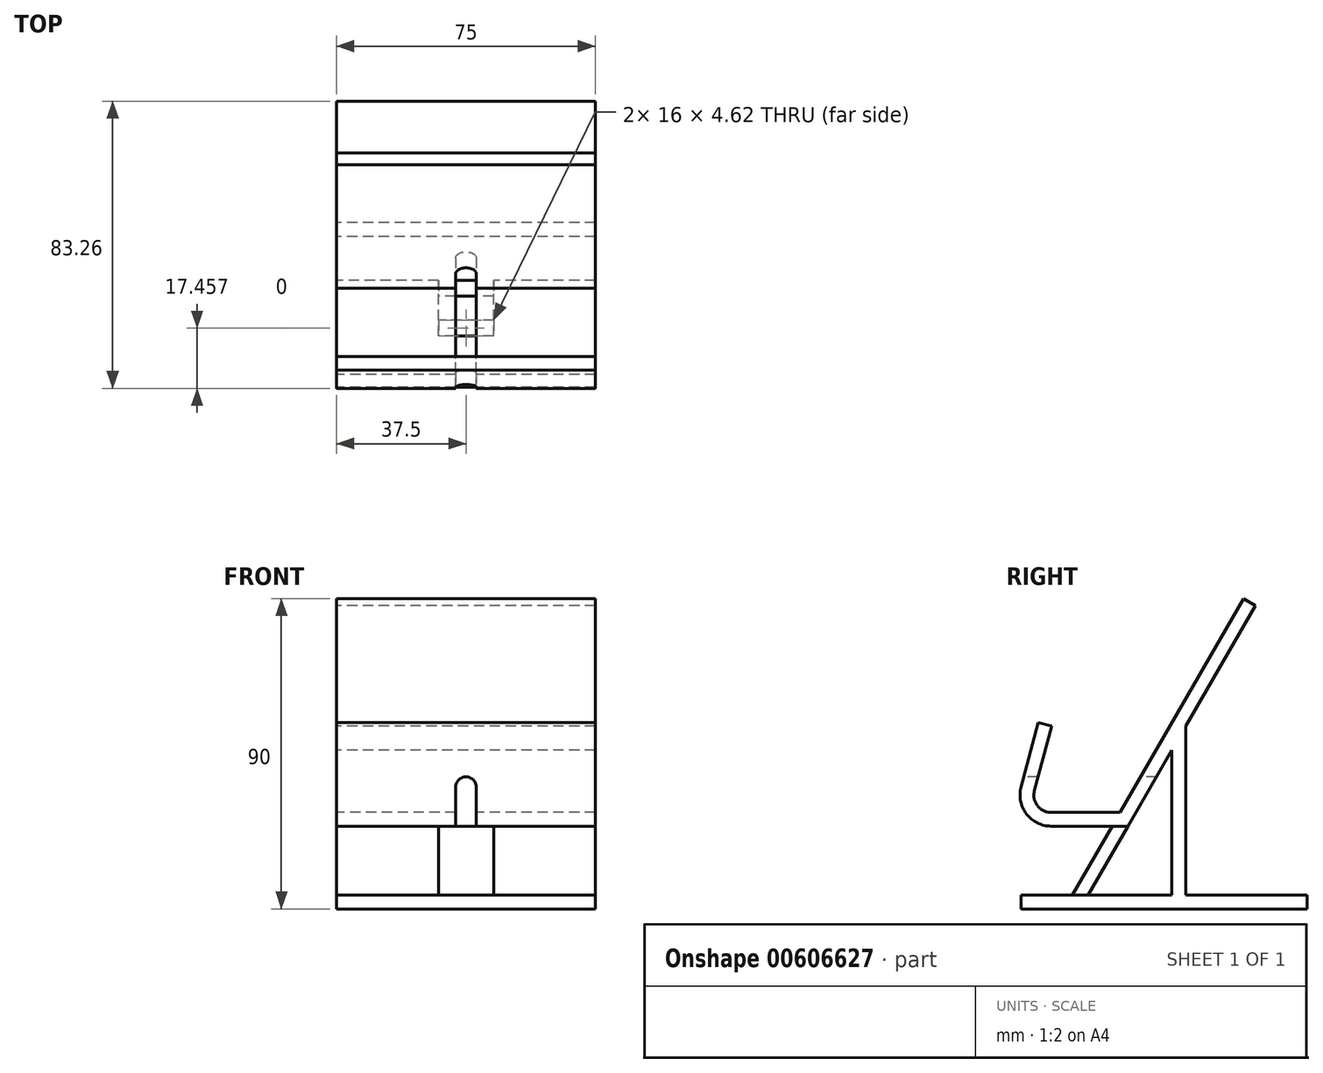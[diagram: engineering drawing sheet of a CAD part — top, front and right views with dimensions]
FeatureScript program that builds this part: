
annotation { "Feature Type Name" : "Feature", "Feature Type Description" : "" }
export const myFeature = defineFeature(function(context is Context, id is Id, definition is map)
    precondition{}
    {
        {
            var Q0;
            Q0=qCreatedBy(makeId("Right.planeOp"),FACE);
            var sketch = newSketch(context, id + "F0", { "sketchPlane" : qUnion([Q0])});
            skLineSegment(sketch, "E0.0", {"start": v(-53.99, -36.2) * mm, "end": v(-48.97, -17.5) * mm});
            skLineSegment(sketch, "E0.1", {"start": v(-29.16, -42.5) * mm, "end": v(-49.16, -42.5) * mm});
            skLineSegment(sketch, "E0.5", {"start": v(-29.16, -42.5) * mm, "end": v(6.64, 19.5) * mm});
            skLineSegment(sketch, "E1.0", {"start": v(-57.85, -35.17) * mm, "end": v(-52.84, -16.47) * mm});
            skArc(sketch, "E1.1", {"start": v(-57.85, -35.17) * mm, "mid": v(-56.3, -42.98) * mm, "end": v(-49.16, -46.5) * mm});
            skLineSegment(sketch, "E2.1", {"start": v(-10.1, -17.5) * mm, "end": v(10.1, 17.5) * mm});
            skLineSegment(sketch, "E2.4", {"start": v(-10.1, -66.5) * mm, "end": v(25.1, -66.5) * mm});
            skLineSegment(sketch, "E3", {"start": v(-52.84, -16.47) * mm, "end": v(-48.97, -17.5) * mm});
            skArc(sketch, "E4.0", {"start": v(-53.99, -36.2) * mm, "mid": v(-53.12, -40.54) * mm, "end": v(-49.16, -42.5) * mm});
            skLineSegment(sketch, "E5", {"start": v(6.64, 19.5) * mm, "end": v(10.1, 17.5) * mm});
            skLineSegment(sketch, "E6", {"start": v(25.1, -66.5) * mm, "end": v(25.1, -70.5) * mm});
            skLineSegment(sketch, "E7", {"start": v(-49.16, -46.5) * mm, "end": v(-31.47, -46.5) * mm});
            skLineSegment(sketch, "E8", {"start": v(-31.47, -46.5) * mm, "end": v(-43.01, -66.5) * mm});
            skLineSegment(sketch, "E9", {"start": v(-43.01, -66.5) * mm, "end": v(-57.85, -66.5) * mm});
            skLineSegment(sketch, "E10", {"start": v(-57.85, -66.5) * mm, "end": v(-57.85, -70.5) * mm});
            skLineSegment(sketch, "E11", {"start": v(-57.85, -70.5) * mm, "end": v(25.1, -70.5) * mm});
            skLineSegment(sketch, "E12", {"start": v(-10.1, -17.5) * mm, "end": v(-10.1, -66.5) * mm});
            skLineSegment(sketch, "E13", {"start": v(-38.4, -66.5) * mm, "end": v(-14.1, -66.5) * mm});
            skLineSegment(sketch, "E14", {"start": v(-14.1, -66.5) * mm, "end": v(-14.1, -24.43) * mm});
            skLineSegment(sketch, "E15", {"start": v(-14.1, -24.43) * mm, "end": v(-38.4, -66.5) * mm});
            skSolve(sketch);
        }
        {
            var Q0;
            Q0=qSketchRegion(id+"F0",true);
            extrude(context, id + "F1", {"entities" : qUnion([Q0]), "endBound" : BoundingType.SYMMETRIC, "depth" : 75 * mm, "offsetDistance" : 25 * mm});
        }
        {
            var Q0;
            Q0=makeQuery(id+"F1.opExtrude","SWEPT_FACE",FACE,{"disambiguationData":[OSD([sQuery(id+"F0.wireOp",EDGE,"E10")])]});
            var sketch = newSketch(context, id + "F2", { "sketchPlane" : qUnion([Q0])});
            skLineSegment(sketch, "E16.bottom", {"start": v(-37.5, -46.5) * mm, "end": v(-8, -46.5) * mm});
            skLineSegment(sketch, "E16.top", {"start": v(-37.5, -66.5) * mm, "end": v(-8, -66.5) * mm});
            skLineSegment(sketch, "E16.left", {"start": v(-37.5, -46.5) * mm, "end": v(-37.5, -66.5) * mm});
            skLineSegment(sketch, "E16.right", {"start": v(-8, -46.5) * mm, "end": v(-8, -66.5) * mm});
            skLineSegment(sketch, "E17.bottom", {"start": v(8, -46.5) * mm, "end": v(37.5, -46.5) * mm});
            skLineSegment(sketch, "E17.top", {"start": v(8, -66.5) * mm, "end": v(37.5, -66.5) * mm});
            skLineSegment(sketch, "E17.left", {"start": v(8, -46.5) * mm, "end": v(8, -66.5) * mm});
            skLineSegment(sketch, "E17.right", {"start": v(37.5, -46.5) * mm, "end": v(37.5, -66.5) * mm});
            skLineSegment(sketch, "E18.bottom", {"start": v(3, -46.5) * mm, "end": v(-3, -46.5) * mm});
            skLineSegment(sketch, "E18.top", {"start": v(3, -35.17) * mm, "end": v(-3, -35.17) * mm});
            skLineSegment(sketch, "E18.left", {"start": v(3, -46.5) * mm, "end": v(3, -35.17) * mm});
            skLineSegment(sketch, "E18.right", {"start": v(-3, -46.5) * mm, "end": v(-3, -35.17) * mm});
            skArc(sketch, "E19", {"start": v(3, -35.17) * mm, "mid": v(0, -32.17) * mm, "end": v(-3, -35.17) * mm});
            skSolve(sketch);
        }
        {
            var Q0;
            Q0 = qSketchRegion(id + "F2", true);
            var Q1;
            Q1=makeQuery(id+"F1.opExtrude","SWEPT_FACE",FACE,{"disambiguationData":[OSD([sQuery(id+"F0.wireOp",EDGE,"E14")])]});
            extrude(context, id + "F3", {"entities" : qUnion([Q0]), "operationType" : NewBodyOperationType.REMOVE, "endBound" : BoundingType.UP_TO_SURFACE, "oppositeDirection" : true, "depth" : 40.4 * mm, "endBoundEntityFace" : qUnion([Q1]), "offsetDistance" : 25 * mm, "hasSecondDirection" : true, "secondDirectionOppositeDirection" : false, "secondDirectionDepth" : 2 * mm});
        }
    });
